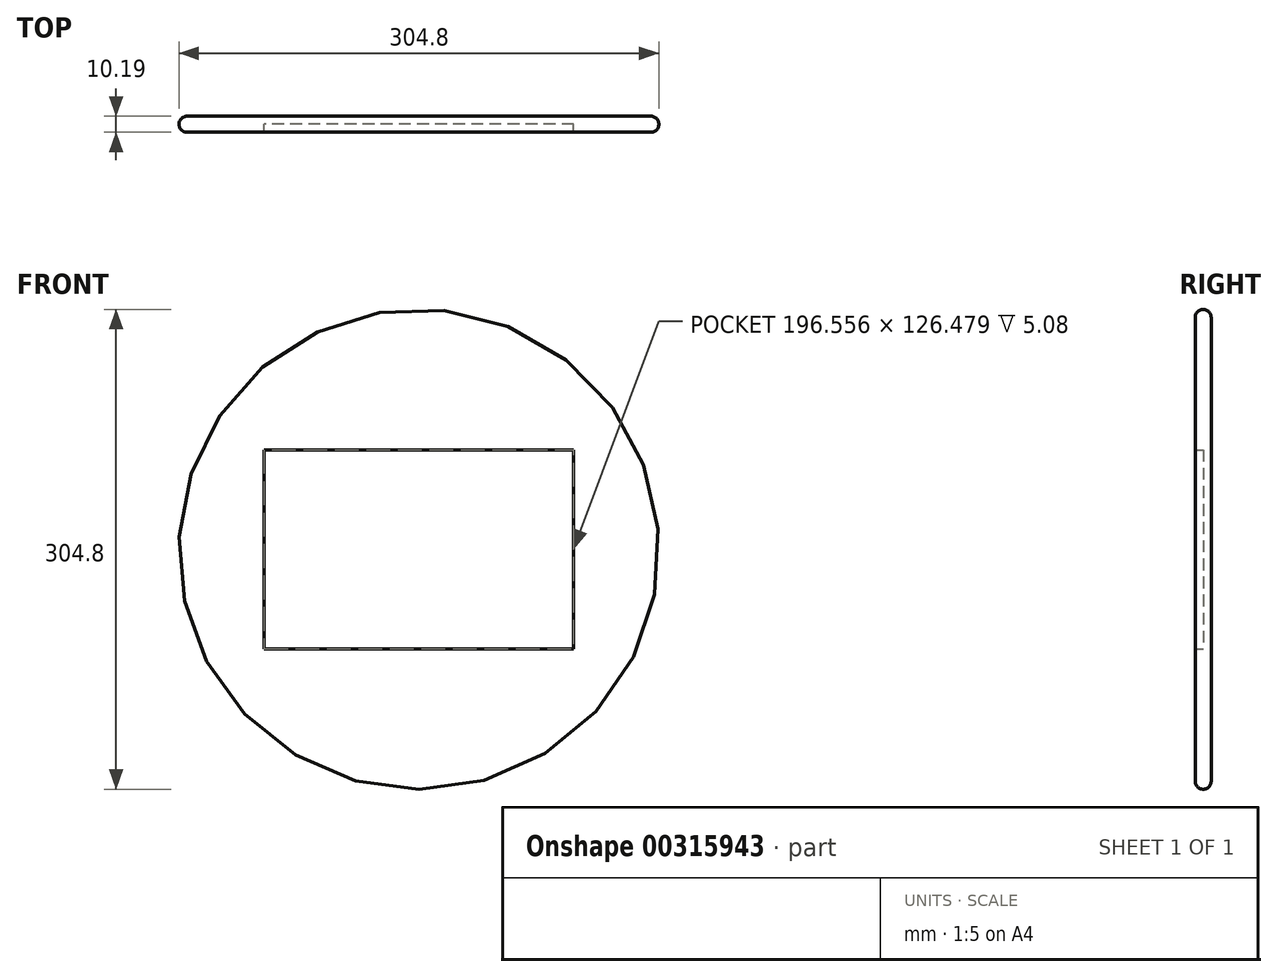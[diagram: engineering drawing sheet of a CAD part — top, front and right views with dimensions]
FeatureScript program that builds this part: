
annotation { "Feature Type Name" : "Feature", "Feature Type Description" : "" }
export const myFeature = defineFeature(function(context is Context, id is Id, definition is map)
    precondition{}
    {
        {
            var Q0;
            Q0=qCreatedBy(makeId("Front.planeOp"),FACE);
            var sketch = newSketch(context, id + "F0", { "sketchPlane" : qUnion([Q0])});
            skCircle(sketch, "E0", {"center": v(0, 0) * mm, "radius": 163.56 * mm});
            skCircle(sketch, "E1", {"center": v(0, 0) * mm, "radius": 152.4 * mm});
            skLineSegment(sketch, "E2.bottom", {"start": v(98.28, 63.24) * mm, "end": v(-98.28, 63.24) * mm});
            skLineSegment(sketch, "E2.top", {"start": v(98.28, -63.24) * mm, "end": v(-98.28, -63.24) * mm});
            skLineSegment(sketch, "E2.left", {"start": v(98.28, 63.24) * mm, "end": v(98.28, -63.24) * mm});
            skLineSegment(sketch, "E2.right", {"start": v(-98.28, 63.24) * mm, "end": v(-98.28, -63.24) * mm});
            skSolve(sketch);
        }
        {
            var Q0;
            Q0=makeQuery(id+"F0.imprint","IMPRINT",FACE,{"disambiguationData":[TD([[makeQuery(id+"F0.imprint","IMPRINT",EDGE,{"derivedFrom":sQuery(id+"F0.wireOp",EDGE,"E1")}),1.0]])]});
            extrude(context, id + "F1", {"entities" : qUnion([Q0]), "endBound" : BoundingType.SYMMETRIC, "depth" : 10.16 * mm});
        }
        {
            var Q0;
            Q0=sQuery(id+"F0.wireOp",EDGE,"E0");
            extrude(context, id + "F2", {"bodyType" : ToolBodyType.SURFACE, "surfaceEntities" : qUnion([Q0]), "endBound" : BoundingType.SYMMETRIC, "depth" : 5.08 * mm});
        }
        {
            var Q0;
            Q0=makeQuery(id+"F1.opExtrude","CAP_EDGE",EDGE,{"disambiguationData":[OSD([sQuery(id+"F0.wireOp",EDGE,"E1")])],"isStart":true});
            var Q1;
            Q1=makeQuery(id+"F1.opExtrude","CAP_EDGE",EDGE,{"disambiguationData":[OSD([sQuery(id+"F0.wireOp",EDGE,"E1")])],"isStart":false});
            fillet(context, id + "F3", {"entities" : qUnion([Q0, Q1]), "radius" : 5.08 * mm, "tangentPropagation" : true, "allowEdgeOverflow" : false});
        }
        {
            var Q0;
            Q0=makeQuery(id+"F0.imprint","IMPRINT",FACE,{"disambiguationData":[TD([[makeQuery(id+"F0.imprint","IMPRINT",EDGE,{"derivedFrom":sQuery(id+"F0.wireOp",EDGE,"E2.bottom")}),1.0]])]});
            extrude(context, id + "F4", {"entities" : qUnion([Q0]), "operationType" : NewBodyOperationType.ADD, "oppositeDirection" : true, "depth" : 5.08 * mm});
        }
        {
            var Q0;
            Q0=makeQuery(id+"F1.opExtrude","CAP_FACE",FACE,{"disambiguationData":[OSD([sQuery(id+"F0.wireOp",EDGE,"E1"),sQuery(id+"F0.wireOp",EDGE,"E2.bottom"),sQuery(id+"F0.wireOp",EDGE,"E2.top"),sQuery(id+"F0.wireOp",EDGE,"E2.left"),sQuery(id+"F0.wireOp",EDGE,"E2.right")])],"isStart":false});
            var sketch = newSketch(context, id + "F5", { "sketchPlane" : qUnion([Q0])});
            skSolve(sketch);
        }
        {
            var Q0;
            Q0=makeQuery(id+"F5.imprint","IMPRINT",FACE,{"disambiguationData":[TD([[makeQuery(id+"F5.imprint","IMPRINT",EDGE,{"derivedFrom":makeQuery(id+"F1.opExtrude","CAP_EDGE",EDGE,{"disambiguationData":[OSD([sQuery(id+"F0.wireOp",EDGE,"E2.bottom")])],"isStart":false})}),1.0]])]});
            extrude(context, id + "F6", {"entities" : qUnion([Q0]), "depth" : 0.03 * mm});
        }
    });
